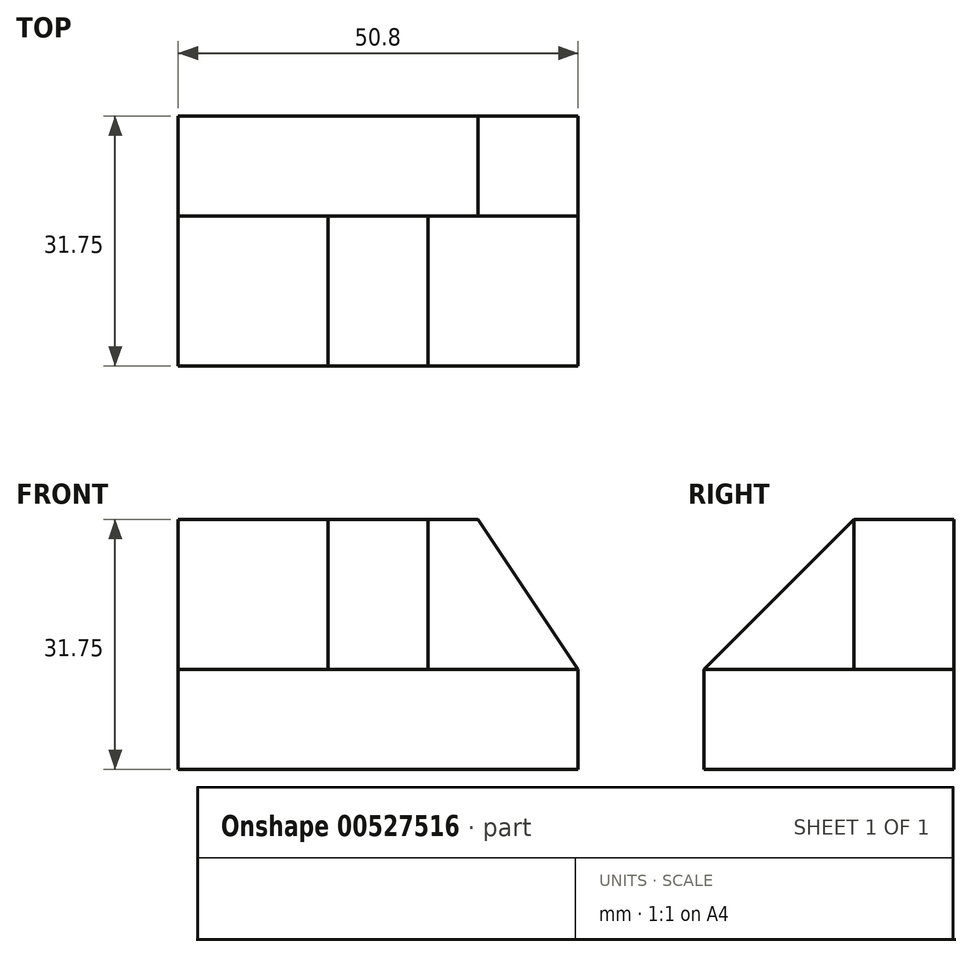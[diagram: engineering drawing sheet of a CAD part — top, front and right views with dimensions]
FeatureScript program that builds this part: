
annotation { "Feature Type Name" : "Feature", "Feature Type Description" : "" }
export const myFeature = defineFeature(function(context is Context, id is Id, definition is map)
    precondition{}
    {
        {
            var Q0;
            Q0=qCreatedBy(makeId("Right.planeOp"),FACE);
            var sketch = newSketch(context, id + "F0", { "sketchPlane" : qUnion([Q0])});
            skLineSegment(sketch, "E0", {"start": v(0, 0) * mm, "end": v(31.75, 0) * mm});
            skLineSegment(sketch, "E1", {"start": v(31.75, 0) * mm, "end": v(31.75, 31.75) * mm});
            skLineSegment(sketch, "E2", {"start": v(31.75, 31.75) * mm, "end": v(19.05, 31.75) * mm});
            skLineSegment(sketch, "E3", {"start": v(19.05, 31.75) * mm, "end": v(19.05, 12.7) * mm});
            skLineSegment(sketch, "E4", {"start": v(19.05, 12.7) * mm, "end": v(0, 12.7) * mm});
            skLineSegment(sketch, "E5", {"start": v(0, 12.7) * mm, "end": v(0, 0) * mm});
            skSolve(sketch);
        }
        {
            var Q0;
            Q0=makeQuery(id+"F0.imprint","IMPRINT",FACE,{"disambiguationData":[TD([[makeQuery(id+"F0.imprint","IMPRINT",EDGE,{"derivedFrom":sQuery(id+"F0.wireOp",EDGE,"E0")}),1.0]])]});
            extrude(context, id + "F1", {"entities" : qUnion([Q0]), "depth" : 50.8 * mm, "offsetDistance" : 25.4 * mm});
        }
        {
            var Q0;
            Q0=makeQuery(id+"F1.opExtrude","SWEPT_FACE",FACE,{"disambiguationData":[OSD([sQuery(id+"F0.wireOp",EDGE,"E3")])]});
            var sketch = newSketch(context, id + "F2", { "sketchPlane" : qUnion([Q0])});
            skLineSegment(sketch, "E6", {"start": v(50.8, 12.7) * mm, "end": v(38.1, 31.75) * mm});
            skLineSegment(sketch, "E7", {"start": v(38.1, 31.75) * mm, "end": v(50.8, 31.75) * mm});
            skLineSegment(sketch, "E8", {"start": v(50.8, 31.75) * mm, "end": v(50.8, 12.7) * mm});
            skLineSegment(sketch, "E9", {"start": v(38.1, 31.75) * mm, "end": v(0, 31.75) * mm});
            skSolve(sketch);
        }
        {
            var Q0;
            Q0=makeQuery(id+"F2.imprint","IMPRINT",FACE,{"disambiguationData":[TD([[makeQuery(id+"F2.imprint","IMPRINT",EDGE,{"derivedFrom":sQuery(id+"F2.wireOp",EDGE,"E6")}),-1.0]])]});
            extrude(context, id + "F3", {"entities" : qUnion([Q0]), "operationType" : NewBodyOperationType.REMOVE, "oppositeDirection" : true, "depth" : 12.7 * mm, "offsetDistance" : 25.4 * mm});
        }
        {
            var Q0;
            Q0=makeQuery(id+"F1.opExtrude","SWEPT_FACE",FACE,{"disambiguationData":[OSD([sQuery(id+"F0.wireOp",EDGE,"E3")])]});
            var sketch = newSketch(context, id + "F4", { "sketchPlane" : qUnion([Q0])});
            skLineSegment(sketch, "E10", {"start": v(0, 12.7) * mm, "end": v(19.05, 12.7) * mm});
            skLineSegment(sketch, "E11", {"start": v(19.05, 12.7) * mm, "end": v(19.05, 31.75) * mm});
            skLineSegment(sketch, "E12", {"start": v(19.05, 31.75) * mm, "end": v(31.75, 31.75) * mm});
            skLineSegment(sketch, "E13", {"start": v(31.75, 31.75) * mm, "end": v(31.75, 12.7) * mm});
            skLineSegment(sketch, "E14", {"start": v(31.75, 12.7) * mm, "end": v(50.8, 12.7) * mm});
            skLineSegment(sketch, "E15", {"start": v(19.05, 12.7) * mm, "end": v(31.75, 12.7) * mm});
            skSolve(sketch);
        }
        {
            var Q0;
            Q0=makeQuery(id+"F4.imprint","IMPRINT",FACE,{"disambiguationData":[TD([[makeQuery(id+"F4.imprint","IMPRINT",EDGE,{"derivedFrom":sQuery(id+"F4.wireOp",EDGE,"E11")}),-1.0]])]});
            extrude(context, id + "F5", {"entities" : qUnion([Q0]), "operationType" : NewBodyOperationType.ADD, "depth" : 19.05 * mm, "offsetDistance" : 25.4 * mm});
        }
        {
            var Q0;
            Q0=makeQuery(id+"F5.opExtrude","SWEPT_FACE",FACE,{"disambiguationData":[OSD([sQuery(id+"F4.wireOp",EDGE,"E11")])]});
            var sketch = newSketch(context, id + "F6", { "sketchPlane" : qUnion([Q0])});
            skLineSegment(sketch, "E16", {"start": v(0, 12.7) * mm, "end": v(-19.05, 31.75) * mm});
            skLineSegment(sketch, "E17", {"start": v(-19.05, 31.75) * mm, "end": v(0, 31.75) * mm});
            skLineSegment(sketch, "E18", {"start": v(0, 31.75) * mm, "end": v(0, 12.7) * mm});
            skSolve(sketch);
        }
        {
            var Q0;
            Q0=makeQuery(id+"F6.imprint","IMPRINT",FACE,{"disambiguationData":[TD([[makeQuery(id+"F6.imprint","IMPRINT",EDGE,{"derivedFrom":sQuery(id+"F6.wireOp",EDGE,"E16")}),-1.0]])]});
            extrude(context, id + "F7", {"entities" : qUnion([Q0]), "operationType" : NewBodyOperationType.REMOVE, "oppositeDirection" : true, "depth" : 25.4 * mm, "offsetDistance" : 25.4 * mm});
        }
    });
